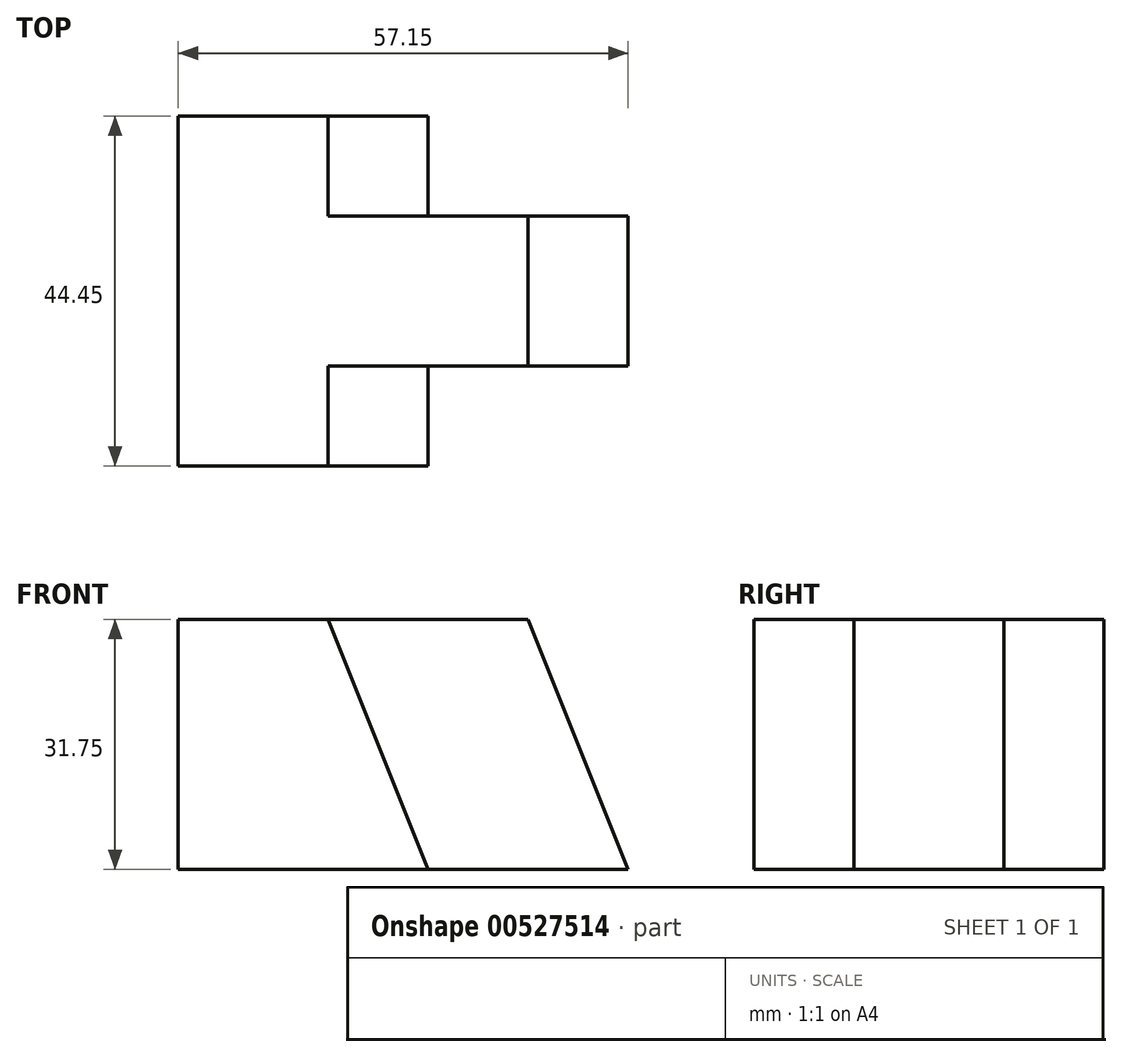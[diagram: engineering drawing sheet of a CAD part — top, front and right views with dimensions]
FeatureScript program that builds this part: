
annotation { "Feature Type Name" : "Feature", "Feature Type Description" : "" }
export const myFeature = defineFeature(function(context is Context, id is Id, definition is map)
    precondition{}
    {
        {
            var Q0;
            Q0=qCreatedBy(makeId("Front.planeOp"),FACE);
            var sketch = newSketch(context, id + "F0", { "sketchPlane" : qUnion([Q0])});
            skLineSegment(sketch, "E0", {"start": v(0, 0) * mm, "end": v(0, 31.75) * mm});
            skLineSegment(sketch, "E1", {"start": v(0, 31.75) * mm, "end": v(57.15, 31.75) * mm});
            skLineSegment(sketch, "E2", {"start": v(57.15, 31.75) * mm, "end": v(57.15, 0) * mm});
            skLineSegment(sketch, "E3", {"start": v(57.15, 0) * mm, "end": v(0, 0) * mm});
            skSolve(sketch);
        }
        {
            var Q0;
            Q0=makeQuery(id+"F0.imprint","IMPRINT",FACE,{"disambiguationData":[TD([[makeQuery(id+"F0.imprint","IMPRINT",EDGE,{"derivedFrom":sQuery(id+"F0.wireOp",EDGE,"E0")}),-1.0]])]});
            extrude(context, id + "F1", {"entities" : qUnion([Q0]), "depth" : 44.45 * mm, "offsetDistance" : 25.4 * mm});
        }
        {
            var Q0;
            Q0=qCreatedBy(makeId("Front.planeOp"),FACE);
            var sketch = newSketch(context, id + "F2", { "sketchPlane" : qUnion([Q0])});
            skLineSegment(sketch, "E4", {"start": v(0, 0) * mm, "end": v(19.05, 0) * mm});
            skLineSegment(sketch, "E5", {"start": v(19.05, 0) * mm, "end": v(19.05, 31.75) * mm});
            skLineSegment(sketch, "E6", {"start": v(19.05, 31.75) * mm, "end": v(0, 31.75) * mm});
            skLineSegment(sketch, "E7", {"start": v(0, 31.75) * mm, "end": v(0, 0) * mm});
            skLineSegment(sketch, "E8", {"start": v(19.05, 31.75) * mm, "end": v(31.75, 0) * mm});
            skPoint(sketch, "E8.endSnap0", {"position": v(9.53, 0) * mm});
            skLineSegment(sketch, "E9", {"start": v(31.75, 0) * mm, "end": v(19.05, 0) * mm});
            skLineSegment(sketch, "E10", {"start": v(31.75, 0) * mm, "end": v(57.15, 0) * mm});
            skSolve(sketch);
        }
        {
            var Q0;
            Q0=makeQuery(id+"F2.imprint","IMPRINT",FACE,{"disambiguationData":[TD([[makeQuery(id+"F2.imprint","IMPRINT",EDGE,{"derivedFrom":sQuery(id+"F2.wireOp",EDGE,"E5")}),-1.0]])]});
            extrude(context, id + "F3", {"entities" : qUnion([Q0]), "operationType" : NewBodyOperationType.REMOVE, "oppositeDirection" : true, "depth" : 12.7 * mm, "offsetDistance" : 25.4 * mm});
        }
        {
            var Q0;
            Q0=makeQuery(id+"F1.opExtrude","CAP_FACE",FACE,{"disambiguationData":[OSD([sQuery(id+"F0.wireOp",EDGE,"E0"),sQuery(id+"F0.wireOp",EDGE,"E1"),sQuery(id+"F0.wireOp",EDGE,"E2"),sQuery(id+"F0.wireOp",EDGE,"E3")])],"isStart":false});
            var sketch = newSketch(context, id + "F4", { "sketchPlane" : qUnion([Q0])});
            skLineSegment(sketch, "E11", {"start": v(57.15, 0) * mm, "end": v(31.75, 0) * mm});
            skLineSegment(sketch, "E12", {"start": v(31.75, 0) * mm, "end": v(19.05, 31.75) * mm});
            skLineSegment(sketch, "E13", {"start": v(19.05, 31.75) * mm, "end": v(57.15, 31.75) * mm});
            skLineSegment(sketch, "E14", {"start": v(57.15, 31.75) * mm, "end": v(57.15, 0) * mm});
            skLineSegment(sketch, "E15", {"start": v(0, 31.75) * mm, "end": v(19.05, 31.75) * mm});
            skSolve(sketch);
        }
        {
            var Q0;
            Q0=makeQuery(id+"F4.imprint","IMPRINT",FACE,{"disambiguationData":[TD([[makeQuery(id+"F4.imprint","IMPRINT",EDGE,{"derivedFrom":sQuery(id+"F4.wireOp",EDGE,"E11")}),-1.0]])]});
            extrude(context, id + "F5", {"entities" : qUnion([Q0]), "operationType" : NewBodyOperationType.REMOVE, "oppositeDirection" : true, "depth" : 12.7 * mm, "offsetDistance" : 25.4 * mm});
        }
        {
            var Q0;
            Q0=makeQuery(id+"F1.opExtrude","CAP_FACE",FACE,{"disambiguationData":[OSD([sQuery(id+"F0.wireOp",EDGE,"E0"),sQuery(id+"F0.wireOp",EDGE,"E1"),sQuery(id+"F0.wireOp",EDGE,"E2"),sQuery(id+"F0.wireOp",EDGE,"E3")])],"isStart":true});
            var sketch = newSketch(context, id + "F6", { "sketchPlane" : qUnion([Q0])});
            skLineSegment(sketch, "E16", {"start": v(-57.15, 0) * mm, "end": v(-31.75, 0) * mm});
            skLineSegment(sketch, "E17", {"start": v(-31.75, 0) * mm, "end": v(-19.05, 31.75) * mm});
            skLineSegment(sketch, "E18", {"start": v(-19.05, 31.75) * mm, "end": v(-57.15, 31.75) * mm});
            skLineSegment(sketch, "E19", {"start": v(-57.15, 31.75) * mm, "end": v(-57.15, 0) * mm});
            skLineSegment(sketch, "E20", {"start": v(-19.05, 31.75) * mm, "end": v(0, 31.75) * mm});
            skSolve(sketch);
        }
        {
            var Q0;
            Q0=makeQuery(id+"F6.imprint","IMPRINT",FACE,{"disambiguationData":[TD([[makeQuery(id+"F6.imprint","IMPRINT",EDGE,{"derivedFrom":sQuery(id+"F6.wireOp",EDGE,"E16")}),1.0]])]});
            extrude(context, id + "F7", {"entities" : qUnion([Q0]), "operationType" : NewBodyOperationType.REMOVE, "oppositeDirection" : true, "depth" : 12.7 * mm, "offsetDistance" : 25.4 * mm});
        }
        {
            var Q0;
            Q0=makeQuery(id+"F5.boolean.opBoolean","COPY",FACE,{"derivedFrom":makeQuery(id+"F5.opExtrude","CAP_FACE",FACE,{"disambiguationData":[OSD([sQuery(id+"F4.wireOp",EDGE,"E11"),sQuery(id+"F4.wireOp",EDGE,"E12"),sQuery(id+"F4.wireOp",EDGE,"E13"),sQuery(id+"F4.wireOp",EDGE,"E14")])],"isStart":false})});
            var sketch = newSketch(context, id + "F8", { "sketchPlane" : qUnion([Q0])});
            skLineSegment(sketch, "E21", {"start": v(57.15, 0) * mm, "end": v(44.45, 31.75) * mm});
            skLineSegment(sketch, "E22", {"start": v(44.45, 31.75) * mm, "end": v(57.15, 31.75) * mm});
            skLineSegment(sketch, "E23", {"start": v(57.15, 31.75) * mm, "end": v(57.15, 0) * mm});
            skLineSegment(sketch, "E24", {"start": v(44.45, 31.75) * mm, "end": v(0, 31.75) * mm});
            skSolve(sketch);
        }
        {
            var Q0;
            Q0=makeQuery(id+"F8.imprint","IMPRINT",FACE,{"disambiguationData":[TD([[makeQuery(id+"F8.imprint","IMPRINT",EDGE,{"derivedFrom":sQuery(id+"F8.wireOp",EDGE,"E21")}),-1.0]])]});
            extrude(context, id + "F9", {"entities" : qUnion([Q0]), "operationType" : NewBodyOperationType.REMOVE, "oppositeDirection" : true, "depth" : 12.7 * mm, "offsetDistance" : 25.4 * mm});
        }
        {
            var Q0;
            Q0=makeQuery(id+"F9.boolean.opBoolean","COPY",FACE,{"derivedFrom":makeQuery(id+"F9.opExtrude","CAP_FACE",FACE,{"disambiguationData":[OSD([sQuery(id+"F8.wireOp",EDGE,"E21"),sQuery(id+"F8.wireOp",EDGE,"E22"),sQuery(id+"F8.wireOp",EDGE,"E23")])],"isStart":false})});
            extrude(context, id + "F10", {"entities" : qUnion([Q0]), "operationType" : NewBodyOperationType.ADD, "depth" : 6.35 * mm, "offsetDistance" : 25.4 * mm});
        }
        {
            var Q0;
            Q0=makeQuery(id+"F10.opExtrude","CAP_FACE",FACE,{"disambiguationData":[OSD([sQuery(id+"F8.wireOp",EDGE,"E21"),sQuery(id+"F8.wireOp",EDGE,"E22"),sQuery(id+"F8.wireOp",EDGE,"E23")])],"isStart":false});
            extrude(context, id + "F11", {"entities" : qUnion([Q0]), "operationType" : NewBodyOperationType.REMOVE, "oppositeDirection" : true, "depth" : 6.35 * mm, "offsetDistance" : 25.4 * mm});
        }
        {
            var Q0;
            Q0=makeQuery(id+"F11.boolean.opBoolean","COPY",FACE,{"derivedFrom":makeQuery(id+"F11.opExtrude","CAP_FACE",FACE,{"disambiguationData":[OSD([sQuery(id+"F8.wireOp",EDGE,"E21"),sQuery(id+"F8.wireOp",EDGE,"E22"),sQuery(id+"F8.wireOp",EDGE,"E23")])],"isStart":false})});
            extrude(context, id + "F12", {"entities" : qUnion([Q0]), "operationType" : NewBodyOperationType.REMOVE, "oppositeDirection" : true, "depth" : 25.4 * mm, "offsetDistance" : 25.4 * mm});
        }
    });
